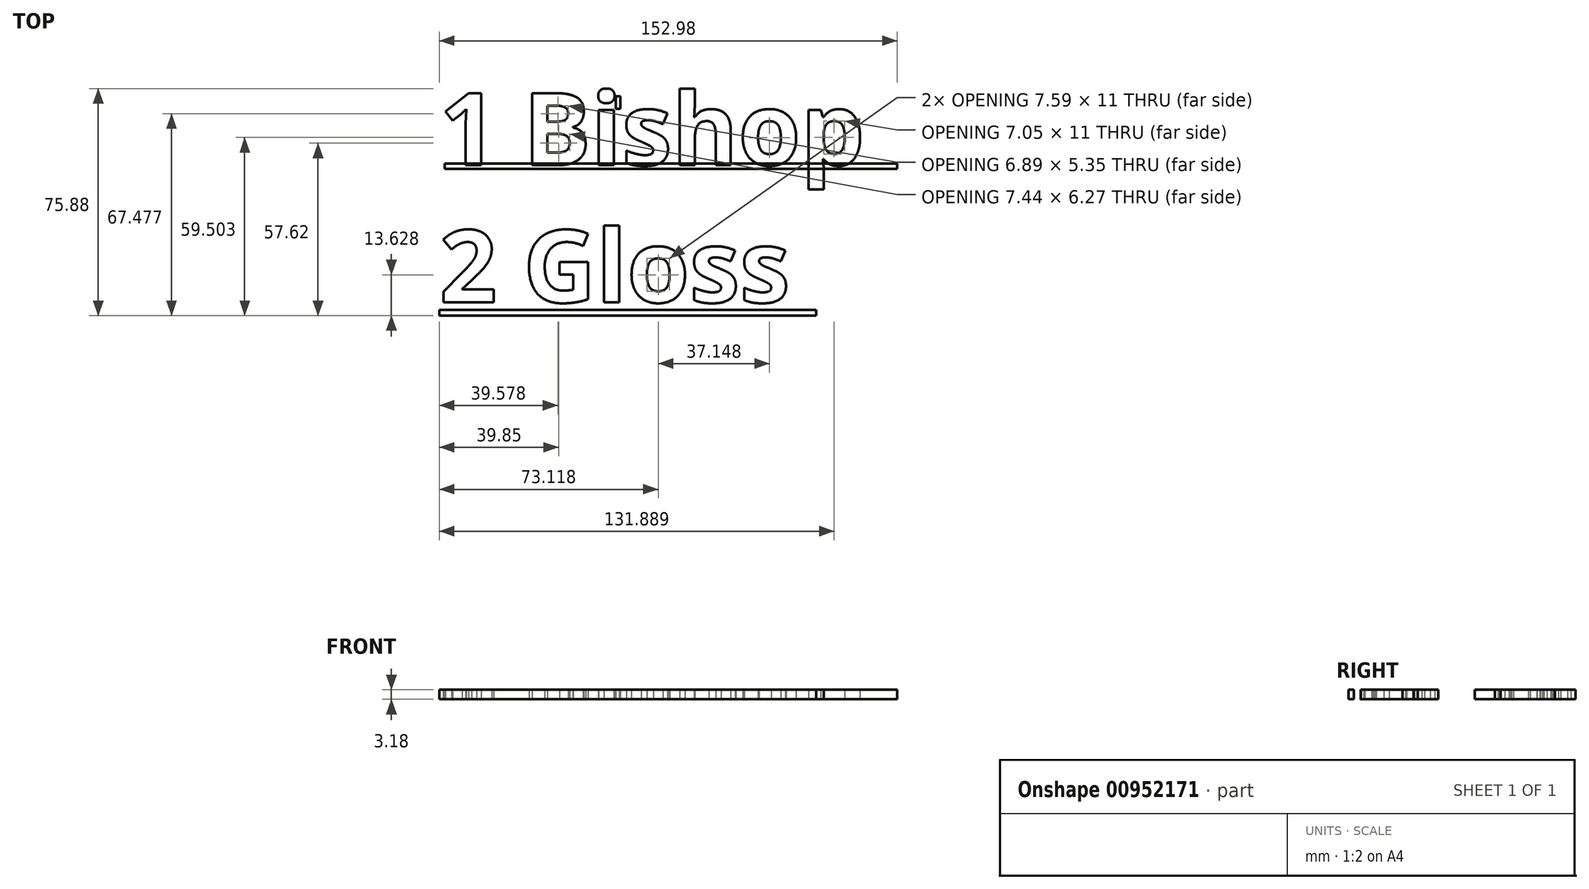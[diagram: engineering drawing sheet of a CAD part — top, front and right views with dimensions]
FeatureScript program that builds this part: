
annotation { "Feature Type Name" : "Feature", "Feature Type Description" : "" }
export const myFeature = defineFeature(function(context is Context, id is Id, definition is map)
    precondition{}
    {
        {
            var Q0;
            Q0=qCreatedBy(makeId("Top.planeOp"),FACE);
            var sketch = newSketch(context, id + "F0", { "sketchPlane" : qUnion([Q0])});
            skText(sketch, "E0", { "text": "1 Bishop\n2 Gloss", "fontName": "OpenSans-Bold.ttf"});
            const initialGuessF0  = {"E0": [0, -0.00204, 1, 0, 0.02427]};
            skSetInitialGuess(sketch, initialGuessF0);
            skSolve(sketch);
        }
        {
            var Q0;
            Q0 = qSketchRegion(id + "F0", true);
            extrude(context, id + "F1", {"entities" : qUnion([Q0]), "flatOperationType" : FlatOperationType.REMOVE, "depth" : 3.17 * mm, "offsetDistance" : 25.4 * mm, "domain" : OperationDomain.MODEL});
        }
        {
            var Q0;
            Q0=qCreatedBy(makeId("Top.planeOp"),FACE);
            var sketch = newSketch(context, id + "F2", { "sketchPlane" : qUnion([Q0])});
            skLineSegment(sketch, "E1.bottom", {"start": v(1.85, -1.5) * mm, "end": v(152.98, -1.5) * mm});
            skLineSegment(sketch, "E1.top", {"start": v(1.85, -3.32) * mm, "end": v(152.98, -3.32) * mm});
            skLineSegment(sketch, "E1.left", {"start": v(1.85, -1.5) * mm, "end": v(1.85, -3.32) * mm});
            skLineSegment(sketch, "E1.right", {"start": v(152.98, -1.5) * mm, "end": v(152.98, -3.32) * mm});
            skLineSegment(sketch, "E2.bottom", {"start": v(0, -50.47) * mm, "end": v(125.87, -50.47) * mm});
            skLineSegment(sketch, "E2.top", {"start": v(0, -52.3) * mm, "end": v(125.87, -52.3) * mm});
            skLineSegment(sketch, "E2.left", {"start": v(0, -50.47) * mm, "end": v(0, -52.3) * mm});
            skLineSegment(sketch, "E2.right", {"start": v(125.87, -50.47) * mm, "end": v(125.87, -52.3) * mm});
            skLineSegment(sketch, "E3.bottom", {"start": v(58.97, 20.91) * mm, "end": v(60.45, 20.91) * mm});
            skLineSegment(sketch, "E3.top", {"start": v(58.97, 16.76) * mm, "end": v(60.45, 16.76) * mm});
            skLineSegment(sketch, "E3.left", {"start": v(58.97, 20.91) * mm, "end": v(58.97, 16.76) * mm});
            skLineSegment(sketch, "E3.right", {"start": v(60.45, 20.91) * mm, "end": v(60.45, 16.76) * mm});
            skSolve(sketch);
        }
        {
            var Q0;
            Q0 = qSketchRegion(id + "F2", true);
            extrude(context, id + "F3", {"entities" : qUnion([Q0]), "flatOperationType" : FlatOperationType.REMOVE, "depth" : 3.17 * mm, "offsetDistance" : 25.4 * mm, "domain" : OperationDomain.MODEL});
        }
    });
